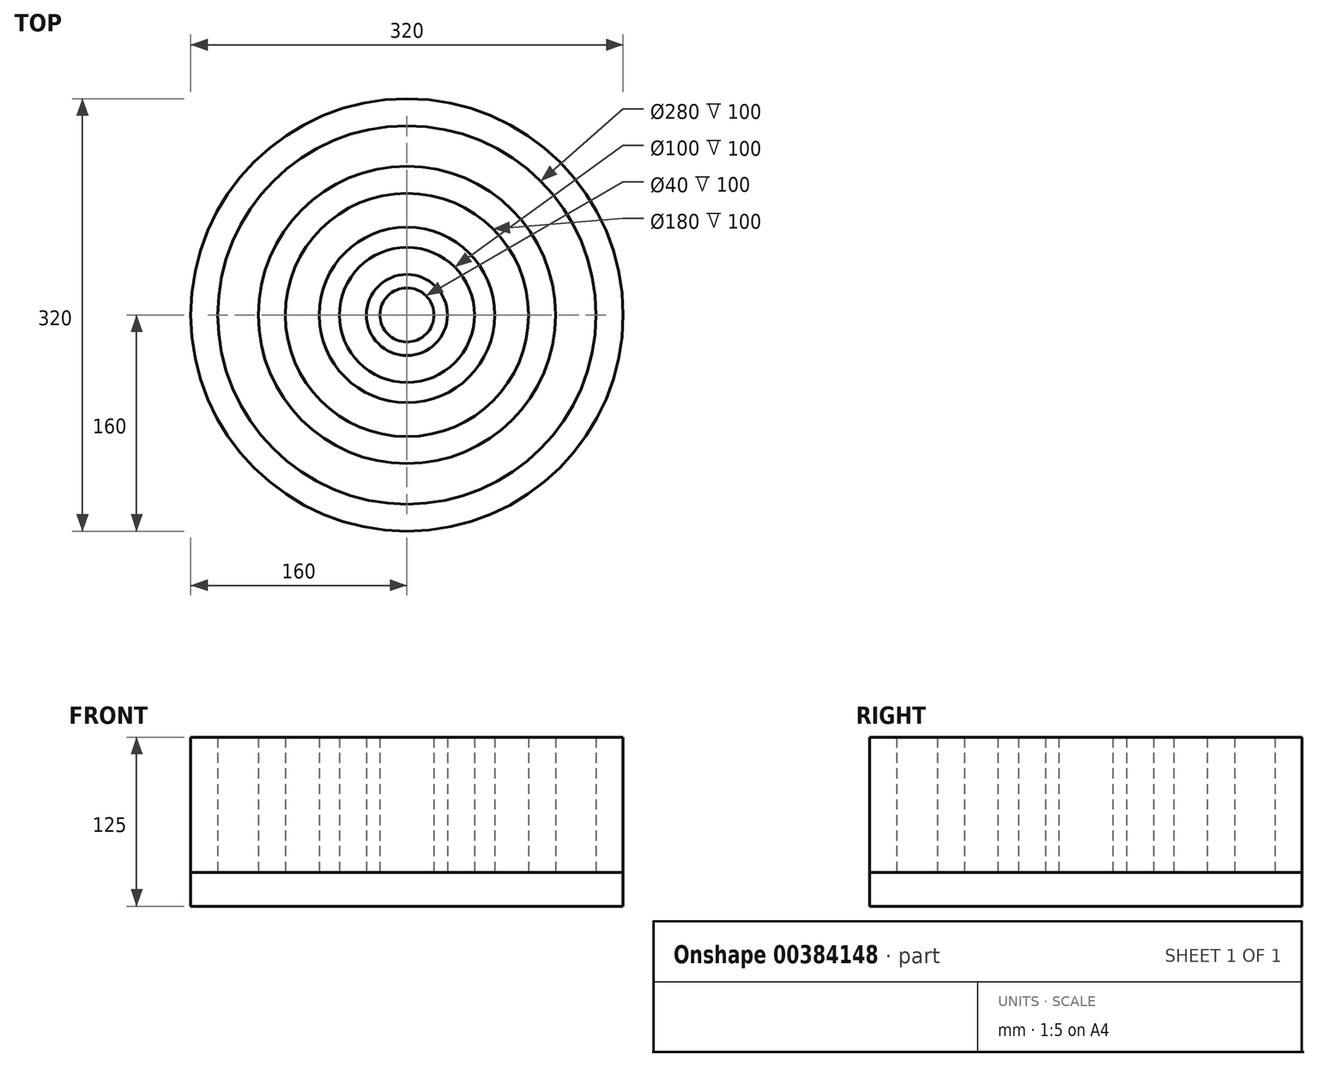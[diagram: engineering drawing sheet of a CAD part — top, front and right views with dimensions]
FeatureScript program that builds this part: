
annotation { "Feature Type Name" : "Feature", "Feature Type Description" : "" }
export const myFeature = defineFeature(function(context is Context, id is Id, definition is map)
    precondition{}
    {
        {
            var Q0;
            Q0=qCreatedBy(makeId("Top.planeOp"),FACE);
            var sketch = newSketch(context, id + "F0", { "sketchPlane" : qUnion([Q0])});
            skCircle(sketch, "E0", {"center": v(0, 0) * mm, "radius": 20 * mm});
            skCircle(sketch, "E1", {"center": v(0, 0) * mm, "radius": 30 * mm});
            skCircle(sketch, "E2", {"center": v(0, 0) * mm, "radius": 50 * mm});
            skCircle(sketch, "E3", {"center": v(0, 0) * mm, "radius": 65 * mm});
            skCircle(sketch, "E4", {"center": v(0, 0) * mm, "radius": 90 * mm});
            skCircle(sketch, "E5", {"center": v(0, 0) * mm, "radius": 110 * mm});
            skCircle(sketch, "E6", {"center": v(0, 0) * mm, "radius": 140 * mm});
            skCircle(sketch, "E7", {"center": v(0, 0) * mm, "radius": 160 * mm});
            skSolve(sketch);
        }
        {
            var Q0;
            Q0 = qSketchRegion(id + "F0", true);
            var Q1;
            Q1=makeQuery(id+"F0.imprint","IMPRINT",FACE,{"disambiguationData":[TD([[makeQuery(id+"F0.imprint","IMPRINT",EDGE,{"derivedFrom":sQuery(id+"F0.wireOp",EDGE,"E2")}),-1.0]])]});
            var Q2;
            Q2=makeQuery(id+"F0.imprint","IMPRINT",FACE,{"disambiguationData":[TD([[makeQuery(id+"F0.imprint","IMPRINT",EDGE,{"derivedFrom":sQuery(id+"F0.wireOp",EDGE,"E0")}),-1.0]])]});
            var Q3;
            Q3=makeQuery(id+"F0.imprint","IMPRINT",FACE,{"disambiguationData":[TD([[makeQuery(id+"F0.imprint","IMPRINT",EDGE,{"derivedFrom":sQuery(id+"F0.wireOp",EDGE,"E4")}),-1.0]])]});
            extrude(context, id + "F1", {"entities" : qUnion([Q0, Q1, Q2, Q3]), "endBound" : BoundingType.SYMMETRIC, "depth" : 100 * mm});
        }
        {
            var Q0;
            Q0=makeQuery(id+"F1.opExtrude","CAP_FACE",FACE,{"disambiguationData":[OSD([sQuery(id+"F0.wireOp",EDGE,"E6"),sQuery(id+"F0.wireOp",EDGE,"E7")])],"isStart":true});
            var sketch = newSketch(context, id + "F2", { "sketchPlane" : qUnion([Q0])});
            skCircle(sketch, "E8.0", {"center": v(0, 0) * mm, "radius": 160 * mm});
            skSolve(sketch);
        }
        {
            var Q0;
            Q0=makeQuery(id+"F2.imprint","IMPRINT",FACE,{"disambiguationData":[TD([[makeQuery(id+"F2.imprint","IMPRINT",EDGE,{"derivedFrom":sQuery(id+"F2.wireOp",EDGE,"E8.0")}),-1.0]])]});
            var sketch = newSketch(context, id + "F3", { "sketchPlane" : qUnion([Q0])});
            skCircle(sketch, "E9", {"center": v(0, 0) * mm, "radius": 160 * mm});
            skSolve(sketch);
        }
        {
            var Q0;
            Q0 = qSketchRegion(id + "F3", true);
            extrude(context, id + "F4", {"entities" : qUnion([Q0]), "depth" : 25 * mm});
        }
    });
